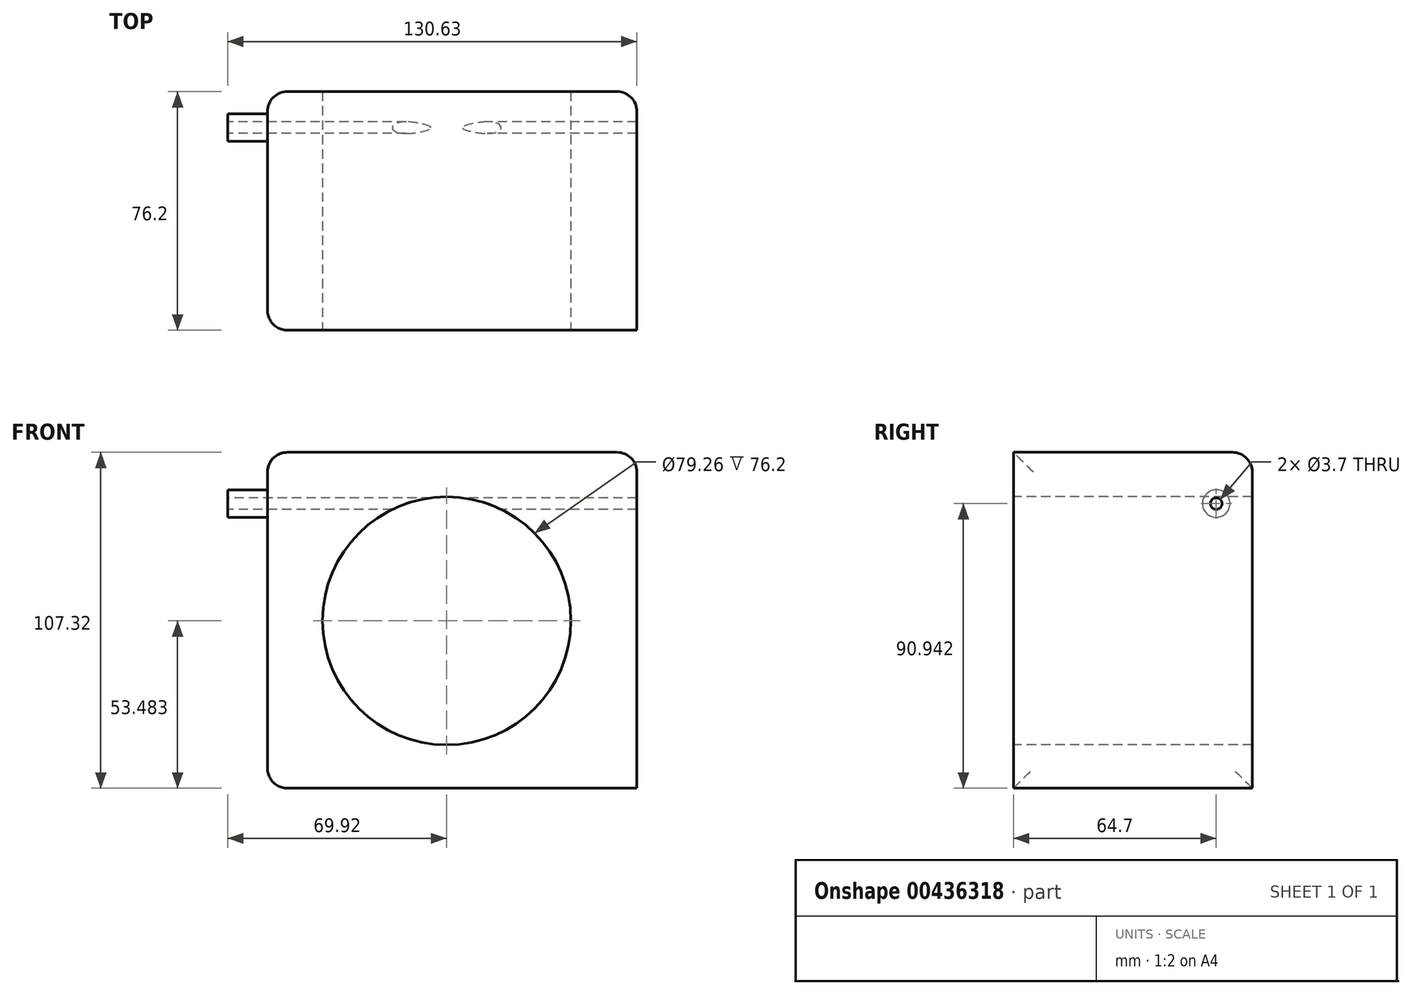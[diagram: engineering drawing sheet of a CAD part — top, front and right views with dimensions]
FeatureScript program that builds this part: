
annotation { "Feature Type Name" : "Feature", "Feature Type Description" : "" }
export const myFeature = defineFeature(function(context is Context, id is Id, definition is map)
    precondition{}
    {
        {
            var Q0;
            Q0=qCreatedBy(makeId("Front.planeOp"),FACE);
            var sketch = newSketch(context, id + "F0", { "sketchPlane" : qUnion([Q0])});
            skLineSegment(sketch, "E0.bottom", {"start": v(-57.22, 37.83) * mm, "end": v(60.71, 37.83) * mm});
            skLineSegment(sketch, "E0.top", {"start": v(-57.22, -69.49) * mm, "end": v(60.71, -69.49) * mm});
            skLineSegment(sketch, "E0.left", {"start": v(-57.22, 37.83) * mm, "end": v(-57.22, -69.49) * mm});
            skLineSegment(sketch, "E0.right", {"start": v(60.71, 37.83) * mm, "end": v(60.71, -69.49) * mm});
            skSolve(sketch);
        }
        {
            var Q0;
            Q0 = qSketchRegion(id + "F0", true);
            extrude(context, id + "F1", {"entities" : qUnion([Q0]), "depth" : 76.2 * mm});
        }
        {
            var Q0;
            Q0=makeQuery(id+"F1.opExtrude","CAP_FACE",FACE,{"disambiguationData":[OSD([sQuery(id+"F0.wireOp",EDGE,"E0.bottom"),sQuery(id+"F0.wireOp",EDGE,"E0.top"),sQuery(id+"F0.wireOp",EDGE,"E0.left"),sQuery(id+"F0.wireOp",EDGE,"E0.right")])],"isStart":false});
            var sketch = newSketch(context, id + "F2", { "sketchPlane" : qUnion([Q0])});
            skCircle(sketch, "E1", {"center": v(0, -16) * mm, "radius": 39.63 * mm});
            skSolve(sketch);
        }
        {
            var Q0;
            Q0 = qSketchRegion(id + "F2", true);
            extrude(context, id + "F3", {"entities" : qUnion([Q0]), "operationType" : NewBodyOperationType.REMOVE, "oppositeDirection" : true, "depth" : 76.2 * mm});
        }
        {
            var Q0;
            Q0=makeQuery(id+"F1.opExtrude","CAP_EDGE",EDGE,{"disambiguationData":[OSD([sQuery(id+"F0.wireOp",EDGE,"E0.bottom")])],"isStart":true});
            var Q1;
            Q1=makeQuery(id+"F3.boolean.opBoolean","COPY",EDGE,{"derivedFrom":makeQuery(id+"F3.opExtrude","CAP_EDGE",EDGE,{"disambiguationData":[OSD([sQuery(id+"F2.wireOp",EDGE,"E1")])],"isStart":false})});
            fillet(context, id + "F4", {"entities" : qUnion([Q0, Q1]), "radius" : 6.35 * mm, "tangentPropagation" : true, "allowEdgeOverflow" : false});
        }
        {
            var Q0;
            Q0=makeQuery(id+"F1.opExtrude","CAP_EDGE",EDGE,{"disambiguationData":[OSD([sQuery(id+"F0.wireOp",EDGE,"E0.right")])],"isStart":true});
            var Q1;
            Q1=makeQuery(id+"F1.opExtrude","SWEPT_FACE",FACE,{"disambiguationData":[OSD([sQuery(id+"F0.wireOp",EDGE,"E0.left")])]});
            fillet(context, id + "F5", {"entities" : qUnion([Q0, Q1]), "radius" : 6.35 * mm, "tangentPropagation" : true, "allowEdgeOverflow" : false});
        }
        {
            var Q0;
            Q0=makeQuery(id+"F1.opExtrude","SWEPT_FACE",FACE,{"disambiguationData":[OSD([sQuery(id+"F0.wireOp",EDGE,"E0.left")])]});
            var sketch = newSketch(context, id + "F6", { "sketchPlane" : qUnion([Q0])});
            skCircle(sketch, "E2", {"center": v(11.5, 21.45) * mm, "radius": 4.39 * mm});
            skSolve(sketch);
        }
        {
            var Q0;
            Q0 = qSketchRegion(id + "F6", true);
            extrude(context, id + "F7", {"entities" : qUnion([Q0]), "operationType" : NewBodyOperationType.ADD, "depth" : 12.7 * mm});
        }
        {
            var Q0;
            Q0=makeQuery(id+"F7.opExtrude","CAP_FACE",FACE,{"disambiguationData":[OSD([sQuery(id+"F6.wireOp",EDGE,"E2")])],"isStart":false});
            var sketch = newSketch(context, id + "F8", { "sketchPlane" : qUnion([Q0])});
            skCircle(sketch, "E3", {"center": v(11.5, 21.45) * mm, "radius": 1.85 * mm});
            skSolve(sketch);
        }
        {
            var Q0;
            Q0 = qSketchRegion(id + "F8", true);
            extrude(context, id + "F9", {"entities" : qUnion([Q0]), "operationType" : NewBodyOperationType.REMOVE, "oppositeDirection" : true, "depth" : 152.4 * mm});
        }
    });
